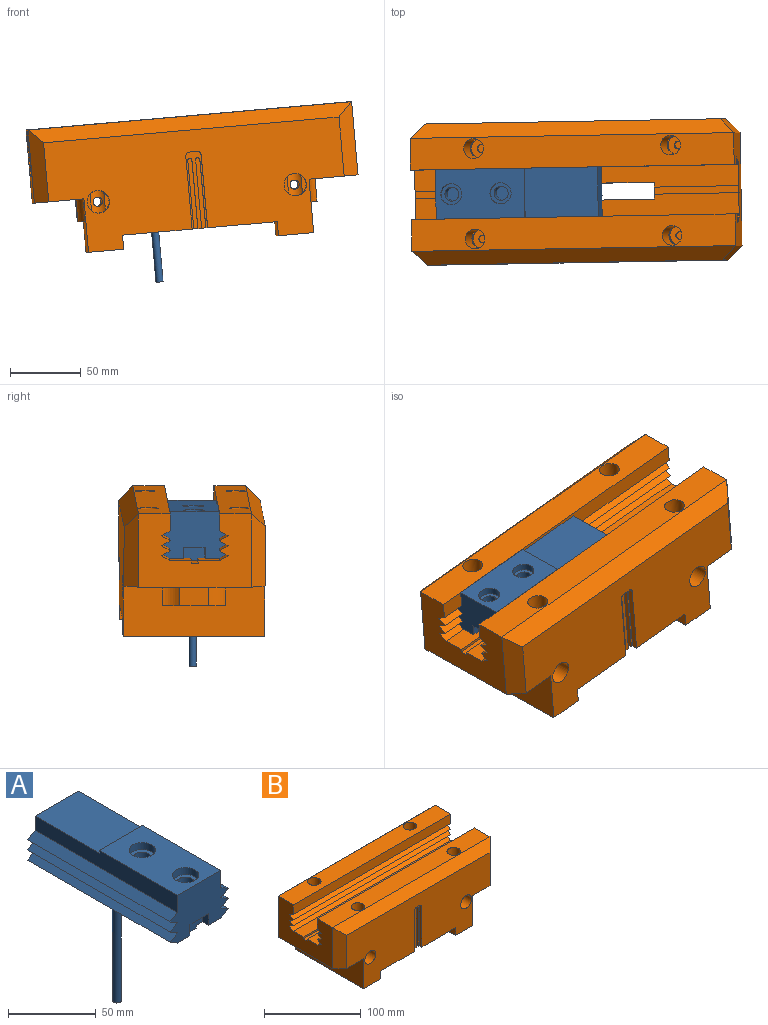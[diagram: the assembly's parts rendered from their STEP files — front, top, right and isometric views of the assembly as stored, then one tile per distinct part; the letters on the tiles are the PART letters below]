
ASSEMBLY  parts=2 mates=2
PART A: 39 faces, bbox 47x115x115.4 mm
  f0: plane 61.5x5mm, normal (0,0,-1), area 297.7mm2, adj f2,f4,f34,f37
  f1: plane 48.5x5mm, normal (0,0,-1), area 232.7mm2, adj f2,f4,f36,f37
  f2: plane 110x2mm, normal (-1,0,0), area 220mm2, adj f0,f1,f10,f34,f36
  f3: plane 115x15mm, normal (0,0,-1), area 1700mm2, adj f4,f7,f19,f31,f34,f36
  f4: plane 110x2mm, normal (1,0,0), area 220mm2, adj f0,f1,f3,f34,f36
  f5: plane 115x12mm, normal (1,0,0), area 1276mm2, adj f7,f8,f9,f22,f35,f36
  f6: plane 115x12mm, normal (-1,0,0), area 1276mm2, adj f7,f8,f9,f13,f35,f36
  f7: plane 47.04x33.3mm, normal (0,-1,0), area 1173.7mm2, adj f3,f5,f6,f9,f10,f11,f12,f13
  f8: plane 35x2mm, normal (0,1,0), area 70mm2, adj f5,f6,f9,f35
  f9: plane 63x35mm, normal (0,0,1), area 1851.6mm2, adj f5,f6,f7,f8,f23,f25
  f10: plane 115x15mm, normal (0,0,-1), area 1700mm2, adj f2,f7,f16,f33,f34,f36
  f11: plane 115x6.02mm, normal (-0.51,0,0.86), area 803.7mm2, adj f7,f12,f14,f36
  f12: plane 115x6.02mm, normal (-0.51,0,-0.86), area 803.7mm2, adj f7,f11,f15,f36
  f13: plane 115x6.02mm, normal (-0.51,0,0.86), area 803.7mm2, adj f6,f7,f14,f36
  f14: plane 115x6.02mm, normal (-0.51,0,-0.86), area 803.7mm2, adj f7,f11,f13,f36
  f15: plane 115x6.02mm, normal (-0.51,0,0.86), area 803.7mm2, adj f7,f12,f16,f36
  f16: plane 115x6.02mm, normal (-0.51,0,-0.86), area 803.7mm2, adj f7,f10,f15,f36
  f17: plane 115x6.02mm, normal (0.51,0,-0.86), area 803.7mm2, adj f7,f18,f20,f36
  f18: plane 115x6.02mm, normal (0.51,0,0.86), area 803.7mm2, adj f7,f17,f21,f36
  f19: plane 115x6.02mm, normal (0.51,0,-0.86), area 803.7mm2, adj f3,f7,f20,f36
  f20: plane 115x6.02mm, normal (0.51,0,0.86), area 803.7mm2, adj f7,f17,f19,f36
  f21: plane 115x6.02mm, normal (0.51,0,-0.86), area 803.7mm2, adj f7,f18,f22,f36
  f22: plane 115x6.02mm, normal (0.51,0,0.86), area 803.7mm2, adj f5,f7,f21,f36
  f23: cylinder r=7.5mm len=15mm, axis (0,0,1), area 235.6mm2, adj f9,f24
  f24: plane 15x15mm, normal (0,0,1), area 98.2mm2, adj f23,f28
  f25: cylinder r=7.5mm len=15mm, axis (0,0,1), area 235.6mm2, adj f9,f26
  f26: plane 15x15mm, normal (0,0,1), area 98.2mm2, adj f25,f30
  f27: plane 10x10mm, normal (0,0,1), area 78.5mm2, adj f28
  f28: cylinder r=5mm len=18mm, axis (0,0,1), area 565.5mm2, adj f24,f27
  f29: plane 10x10mm, normal (0,0,1), area 78.5mm2, adj f30
  f30: cylinder r=5mm len=18mm, axis (0,0,1), area 565.5mm2, adj f26,f29
  f31: plane 8x5mm, normal (-1,0,0), area 40mm2, adj f3,f7,f32,f34
  f32: plane 15x5mm, normal (0,0,-1), area 75mm2, adj f7,f31,f33,f34
  f33: plane 8x5mm, normal (1,0,0), area 40mm2, adj f7,f10,f32,f34
  f34: plane 15x10mm, normal (0,-1,0), area 130mm2, adj f0,f2,f3,f4,f10,f31,f32,f33
  f35: plane 52x35mm, normal (0,0,1), area 1820mm2, adj f5,f6,f8,f36
  f36: plane 47.04x33.3mm, normal (0,1,0), area 1233.7mm2, adj f1,f2,f3,f4,f5,f6,f10,f11
  f37: cylinder r=2.5mm len=80.1mm, axis (0,0,1), area 1258.2mm2, adj f0,f1,f38
  f38: plane 5x5mm, normal (0,0,-1), area 19.6mm2, adj f37
PART B: 102 faces, bbox 230x100x90 mm
  f0: plane 110x44mm, normal (0,0,-1), area 4772mm2, adj f20,f80,f81,f86,f90,f91,f92,f94
  f1: plane 230x15mm, normal (0,0,1), area 3065mm2, adj f2,f19,f21,f29,f30,f80,f81,f100
  f2: plane 60x2mm, normal (0,1,0), area 120mm2, adj f1,f3,f19,f81
  f3: plane 60x5mm, normal (0,0,1), area 300mm2, adj f2,f4,f19,f81
  f4: plane 60x2mm, normal (0,-1,0), area 120mm2, adj f3,f5,f19,f81
  f5: plane 230x15mm, normal (0,0,1), area 3065mm2, adj f4,f19,f21,f32,f33,f80,f81,f101
  f6: plane 110x44mm, normal (0,0,-1), area 4840mm2, adj f18,f80,f81,f101
  f7: plane 20x16mm, normal (1,0,0), area 320mm2, adj f8,f9,f84,f85
  f8: plane 45x5mm, normal (0,0,-1), area 139.6mm2, adj f7,f10,f84,f85
  f9: plane 100x35mm, normal (0,0,-1), area 3260.4mm2, adj f7,f10,f18,f20,f21,f40,f43,f84
  f10: plane 100x38mm, normal (1,0,0), area 3080mm2, adj f8,f9,f16,f18,f20,f84,f85
  f11: plane 20x16mm, normal (-1,0,0), area 320mm2, adj f12,f13,f82,f83
  f12: plane 45x5mm, normal (0,0,-1), area 139.1mm2, adj f11,f14,f82,f83
  f13: plane 100x35mm, normal (0,0,-1), area 3260.9mm2, adj f11,f14,f18,f19,f20,f42,f45,f82
  f14: plane 100x38mm, normal (-1,0,0), area 3080mm2, adj f12,f13,f15,f18,f20,f82,f83
  f15: plane 100x25mm, normal (0,0,-1), area 2500mm2, adj f14,f18,f20,f81
  f16: plane 100x25mm, normal (0,0,-1), area 2500mm2, adj f10,f18,f20,f80
  f17: plane 230x22.5mm, normal (0,0,1), area 4867.1mm2, adj f19,f21,f37,f41,f53,f56
  f18: plane 210x80mm, normal (0,1,0), area 13397.9mm2, adj f6,f9,f10,f13,f14,f15,f16,f40
  f19: plane 80x52mm, normal (-1,0,0), area 2856.3mm2, adj f1,f2,f3,f4,f5,f13,f17,f22
  f20: plane 210x80mm, normal (0,-1,0), area 12802.2mm2, adj f0,f9,f10,f13,f14,f15,f16,f43
  f21: plane 80x52mm, normal (1,0,0), area 2856.3mm2, adj f1,f5,f9,f17,f22,f23,f24,f25
  f22: plane 230x22.5mm, normal (0,0,1), area 4867.1mm2, adj f19,f21,f23,f44,f46,f49
  f23: plane 230x12mm, normal (0,1,0), area 2760mm2, adj f19,f21,f22,f24
  f24: plane 230x6.02mm, normal (0,0.51,-0.86), area 1607.4mm2, adj f19,f21,f23,f25
  f25: plane 230x6.02mm, normal (0,0.51,0.86), area 1607.4mm2, adj f19,f21,f24,f26
  f26: plane 230x6.02mm, normal (0,0.51,-0.86), area 1607.4mm2, adj f19,f21,f25,f27
  f27: plane 230x6.02mm, normal (0,0.51,0.86), area 1607.4mm2, adj f19,f21,f26,f28
  f28: plane 230x6.02mm, normal (0,0.51,-0.86), area 1607.4mm2, adj f19,f21,f27,f29
  f29: plane 230x6.02mm, normal (0,0.51,0.86), area 1607.4mm2, adj f1,f19,f21,f28
  f30: plane 60x2mm, normal (0,1,0), area 120mm2, adj f1,f21,f31,f80
  f31: plane 60x5mm, normal (0,0,1), area 300mm2, adj f21,f30,f32,f80
  f32: plane 60x2mm, normal (0,-1,0), area 120mm2, adj f5,f21,f31,f80
  f33: plane 230x6.02mm, normal (0,-0.51,0.86), area 1607.4mm2, adj f5,f19,f21,f34
  f34: plane 230x6.02mm, normal (0,-0.51,-0.86), area 1607.4mm2, adj f19,f21,f33,f35
  f35: plane 230x6.02mm, normal (0,-0.51,0.86), area 1607.4mm2, adj f19,f21,f34,f36
  f36: plane 230x6.02mm, normal (0,-0.51,-0.86), area 1607.4mm2, adj f19,f21,f35,f38
  f37: plane 230x12mm, normal (0,-1,0), area 2760mm2, adj f17,f19,f21,f39
  f38: plane 230x6.02mm, normal (0,-0.51,0.86), area 1607.4mm2, adj f19,f21,f36,f39
  f39: plane 230x6.02mm, normal (0,-0.51,-0.86), area 1607.4mm2, adj f19,f21,f37,f38
  f40: plane 52x10mm, normal (0.71,0.71,0), area 664.7mm2, adj f9,f18,f21,f41
  f41: plane 230x10mm, normal (0,0.71,0.71), area 3111.3mm2, adj f17,f18,f40,f42
  f42: plane 52x10mm, normal (-0.71,0.71,0), area 664.7mm2, adj f13,f18,f19,f41
  f43: plane 52x10mm, normal (0.71,-0.71,0), area 664.7mm2, adj f9,f20,f21,f44
  f44: plane 230x10mm, normal (0,-0.71,0.71), area 3111.3mm2, adj f20,f22,f43,f45
  f45: plane 52x10mm, normal (-0.71,-0.71,0), area 664.7mm2, adj f13,f19,f20,f44
  f46: cylinder r=7mm len=63mm, axis (0,0,1), area 2339mm2, adj f22,f47,f48,f72,f77,f78,f79
  f47: cylinder r=7mm len=7mm, axis (0,0,1), area 20.7mm2, adj f46,f48,f79
  f48: plane 14x14mm, normal (0,0,1), area 129.3mm2, adj f46,f47,f64
  f49: cylinder r=7mm len=63mm, axis (0,0,1), area 2339mm2, adj f22,f50,f51,f73,f74,f75,f76
  f50: cylinder r=7mm len=7mm, axis (0,0,1), area 20.7mm2, adj f49,f51,f76
  f51: plane 14x14mm, normal (0,0,1), area 129.3mm2, adj f49,f50,f62
  f52: cylinder r=7mm len=7mm, axis (0,0,1), area 20.7mm2, adj f53,f54,f71
  f53: cylinder r=7mm len=63mm, axis (0,0,1), area 2338.9mm2, adj f17,f52,f54,f69,f70,f71,f73
  f54: plane 14x14mm, normal (0,0,1), area 129.3mm2, adj f52,f53,f60
  f55: cylinder r=7mm len=7mm, axis (0,0,1), area 20.7mm2, adj f56,f57,f68
  f56: cylinder r=7mm len=63mm, axis (0,0,1), area 2338.9mm2, adj f17,f55,f57,f66,f67,f68,f72
  f57: plane 14x14mm, normal (0,0,1), area 129.3mm2, adj f55,f56,f58
  f58: cylinder r=2.8mm len=5.6mm, axis (0,0,1), area 88mm2, adj f57,f59
  f59: plane 5.6x5.6mm, normal (0,0,1), area 24.6mm2, adj f58
  f60: cylinder r=2.8mm len=5.6mm, axis (0,0,1), area 88mm2, adj f54,f61
  f61: plane 5.6x5.6mm, normal (0,0,1), area 24.6mm2, adj f60
  f62: cylinder r=2.8mm len=5.6mm, axis (0,0,1), area 88mm2, adj f51,f63
  f63: plane 5.6x5.6mm, normal (0,0,1), area 24.6mm2, adj f62
  f64: cylinder r=2.8mm len=5.6mm, axis (0,0,1), area 88mm2, adj f48,f65
  f65: plane 5.6x5.6mm, normal (0,0,1), area 24.6mm2, adj f64
  f66: plane 12.65x3.1mm, normal (0,1,0), area 27.4mm2, adj f56,f68
  f67: plane 12.65x3.1mm, normal (0,1,0), area 27.4mm2, adj f56,f68
  f68: cylinder r=8mm len=23mm, axis (0,1,0), area 831.6mm2, adj f18,f55,f56,f66,f67
  f69: plane 12.65x3.1mm, normal (0,1,0), area 27.4mm2, adj f53,f71
  f70: plane 12.65x3.1mm, normal (0,1,0), area 27.4mm2, adj f53,f71
  f71: cylinder r=8mm len=23mm, axis (0,1,0), area 831.6mm2, adj f18,f52,f53,f69,f70
  f72: cylinder r=3.25mm len=51.6mm, axis (0,1,0), area 1037.1mm2, adj f46,f56
  f73: cylinder r=3.25mm len=51.6mm, axis (0,1,0), area 1037.1mm2, adj f49,f53
  f74: plane 12.65x3.1mm, normal (0,-1,0), area 27.4mm2, adj f49,f76
  f75: plane 12.65x3.1mm, normal (0,-1,0), area 27.4mm2, adj f49,f76
  f76: cylinder r=8mm len=23mm, axis (0,-1,0), area 831.6mm2, adj f20,f49,f50,f74,f75
  f77: plane 12.65x3.1mm, normal (0,-1,0), area 27.4mm2, adj f46,f79
  f78: plane 12.65x3.1mm, normal (0,-1,0), area 27.4mm2, adj f46,f79
  f79: cylinder r=8mm len=23mm, axis (0,-1,0), area 831.6mm2, adj f20,f46,f47,f77,f78
  f80: plane 100x56.7mm, normal (-1,0,0), area 1550.4mm2, adj f0,f1,f5,f6,f16,f18,f20,f30
  f81: plane 100x56.7mm, normal (1,0,0), area 1550.4mm2, adj f0,f1,f2,f3,f4,f5,f6,f15
  f82: cylinder r=18.12mm len=16mm, axis (0,0,-1), area 220.7mm2, adj f11,f12,f13,f14
  f83: cylinder r=18.12mm len=16mm, axis (0,0,-1), area 220.7mm2, adj f11,f12,f13,f14
  f84: cylinder r=18.9mm len=16mm, axis (0,0,-1), area 225.1mm2, adj f7,f8,f9,f10
  f85: cylinder r=18.12mm len=16mm, axis (0,0,-1), area 215.8mm2, adj f7,f8,f9,f10
  f86: plane 51.5x4mm, normal (-1,0,0), area 206mm2, adj f0,f20,f87,f91
  f87: cylinder r=3mm len=4mm, axis (0,-1,0), area 18.8mm2, adj f20,f86,f88,f91
  f88: plane 5x4mm, normal (0,0,-1), area 20mm2, adj f20,f87,f89,f91
  f89: cylinder r=3mm len=4mm, axis (0,-1,0), area 18.8mm2, adj f20,f88,f90,f91
  f90: plane 51.5x4mm, normal (1,0,0), area 206mm2, adj f0,f20,f89,f91
  f91: plane 54.5x11mm, normal (0,-1,0), area 297.6mm2, adj f0,f86,f87,f88,f89,f90,f92,f93
  f92: plane 48.5x4mm, normal (-1,0,0), area 194mm2, adj f0,f91,f93,f95
  f93: cylinder r=1.5mm len=4mm, axis (0,-1,0), area 18.8mm2, adj f91,f92,f94,f95
  f94: plane 48.5x4mm, normal (1,0,0), area 194mm2, adj f0,f91,f93,f95
  f95: plane 50x3mm, normal (0,-1,0), area 149mm2, adj f0,f92,f93,f94
  f96: plane 48.5x4mm, normal (-1,0,0), area 194mm2, adj f0,f91,f97,f99
  f97: cylinder r=1.5mm len=4mm, axis (0,-1,0), area 18.8mm2, adj f91,f96,f98,f99
  f98: plane 48.5x4mm, normal (1,0,0), area 194mm2, adj f0,f91,f97,f99
  f99: plane 50x3mm, normal (0,-1,0), area 149mm2, adj f0,f96,f97,f98
  f100: plane 110x46.7mm, normal (0,1,0), area 5137mm2, adj f0,f1,f80,f81
  f101: plane 110x46.7mm, normal (0,-1,0), area 5137mm2, adj f5,f6,f80,f81
PLACE A rot(axis=(0.04,-0.04,-1),89.1deg) t=(-29.13,-32.3,33.52)mm
PLACE B rot(axis=(0.01,-0.98,0.2),5.1deg) t=(5.1,-31.21,36.51)mm
MATE planar A.f0 <-> B.f3  axis (0.09,0,-1) through (-54.18,-32.26,-4.11)mm
MATE planar A.f5 <-> B.f23  axis (0.02,-1,0) through (-36.31,-49.44,26.43)mm
